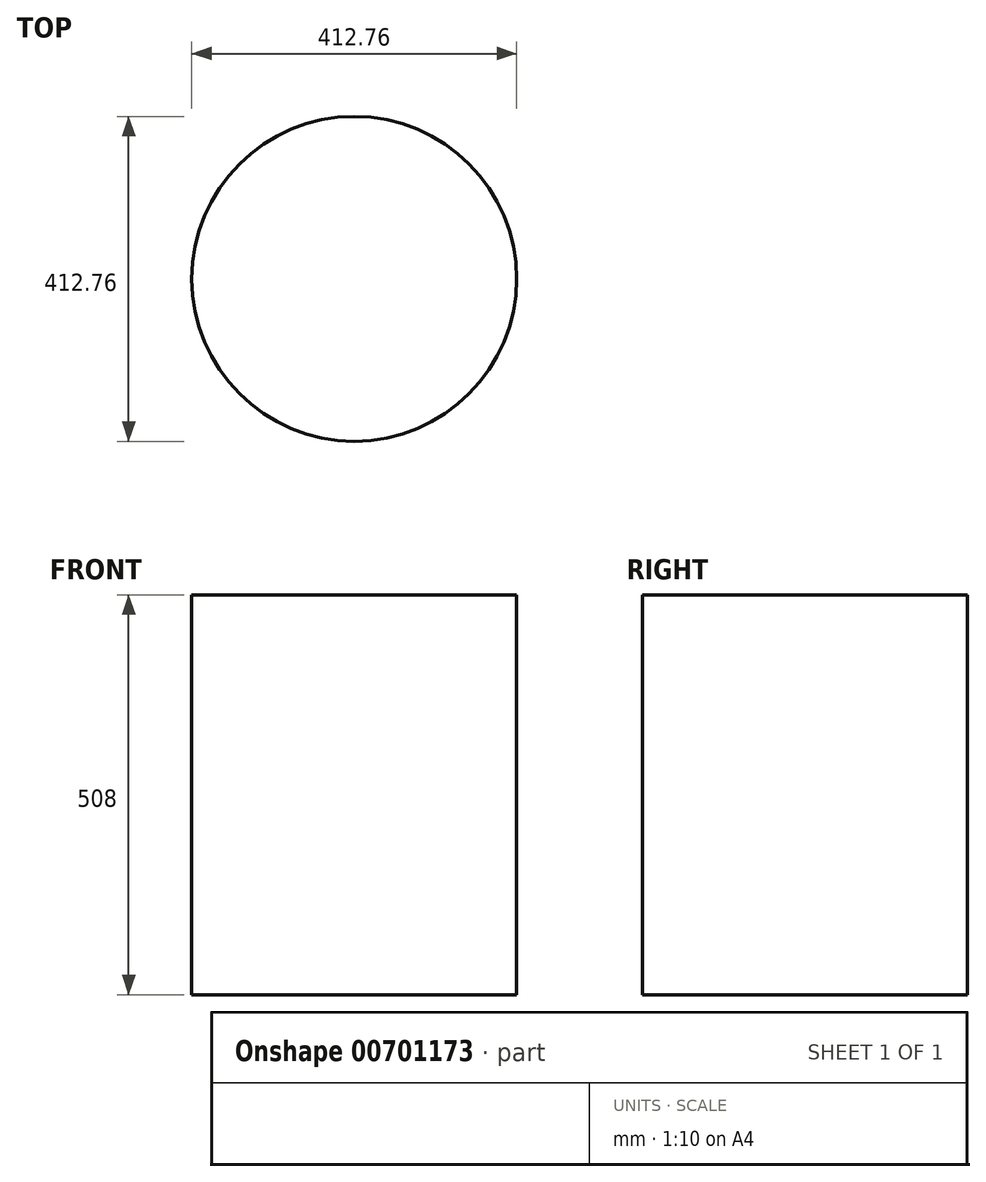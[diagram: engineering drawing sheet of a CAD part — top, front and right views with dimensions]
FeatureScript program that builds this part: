
annotation { "Feature Type Name" : "Feature", "Feature Type Description" : "" }
export const myFeature = defineFeature(function(context is Context, id is Id, definition is map)
    precondition{}
    {
        {
            var Q0;
            Q0=qCreatedBy(makeId("Top.planeOp"),FACE);
            var sketch = newSketch(context, id + "F0", { "sketchPlane" : qUnion([Q0])});
            skCircle(sketch, "E0", {"center": v(0, 0) * mm, "radius": 206.38 * mm});
            skSolve(sketch);
        }
        {
            var Q0;
            Q0 = qSketchRegion(id + "F0", true);
            extrude(context, id + "F1", {"entities" : qUnion([Q0]), "depth" : 508 * mm, "offsetDistance" : 25.4 * mm});
        }
    });
